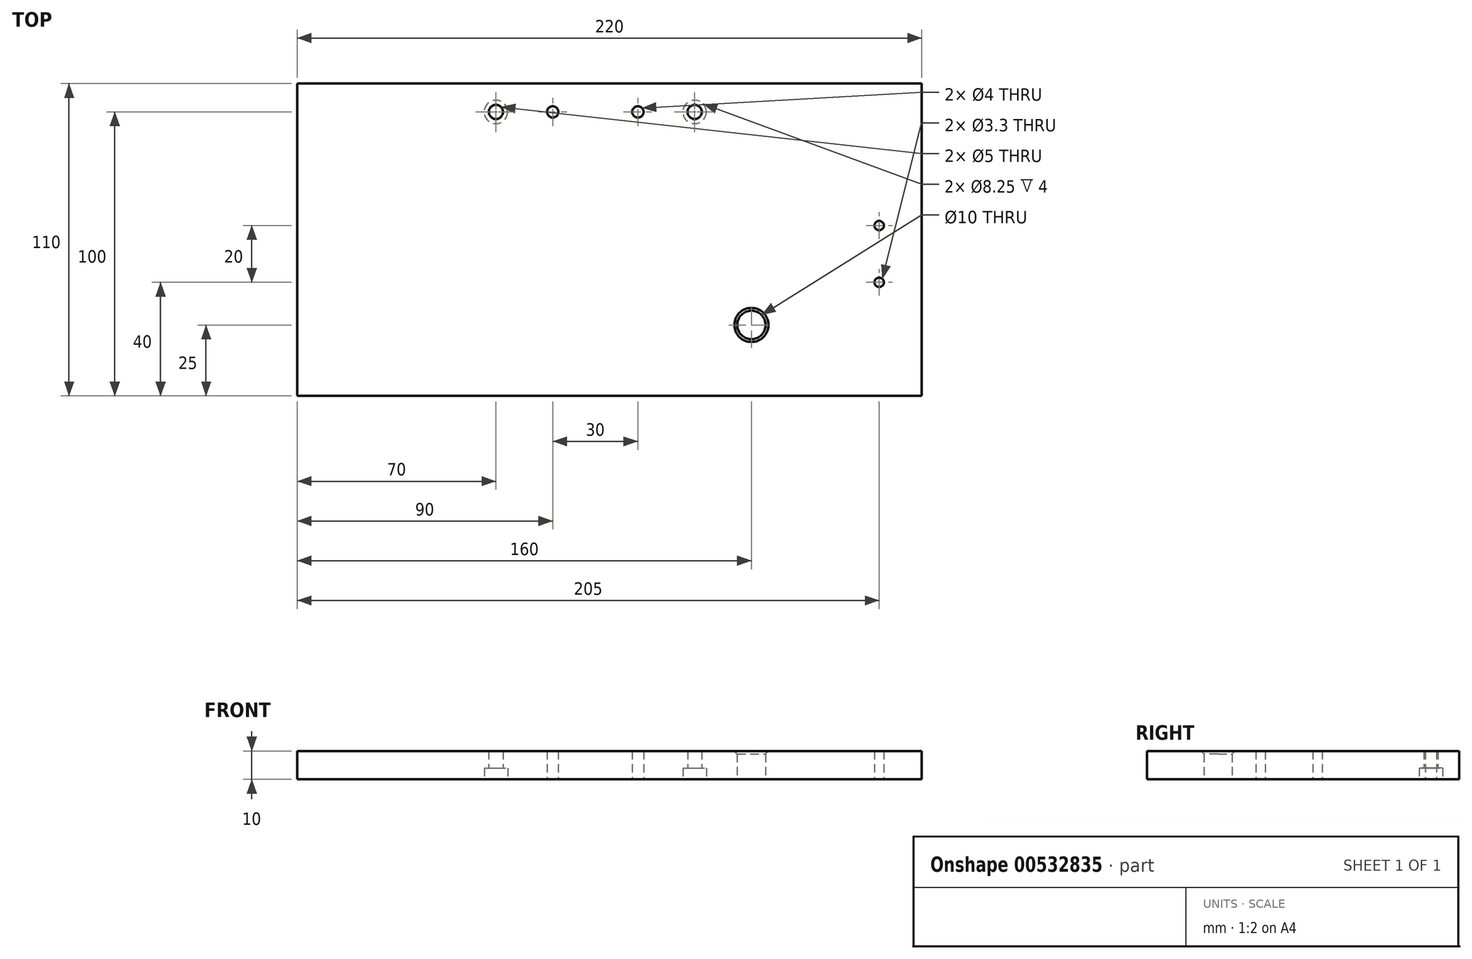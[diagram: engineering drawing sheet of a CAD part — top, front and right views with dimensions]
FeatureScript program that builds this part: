
annotation { "Feature Type Name" : "Feature", "Feature Type Description" : "" }
export const myFeature = defineFeature(function(context is Context, id is Id, definition is map)
    precondition{}
    {
        {
            var Q0;
            Q0=qCreatedBy(makeId("Top.planeOp"),FACE);
            var sketch = newSketch(context, id + "F0", { "sketchPlane" : qUnion([Q0])});
            skLineSegment(sketch, "E0.bottom", {"start": v(-110, 55) * mm, "end": v(110, 55) * mm});
            skLineSegment(sketch, "E0.top", {"start": v(-110, -55) * mm, "end": v(110, -55) * mm});
            skLineSegment(sketch, "E0.left", {"start": v(-110, 55) * mm, "end": v(-110, -55) * mm});
            skLineSegment(sketch, "E0.right", {"start": v(110, 55) * mm, "end": v(110, -55) * mm});
            skSolve(sketch);
        }
        {
            var Q0;
            Q0 = qSketchRegion(id + "F0", true);
            extrude(context, id + "F1", {"entities" : qUnion([Q0]), "depth" : 10 * mm, "offsetDistance" : 25 * mm});
        }
        {
            var Q0;
            Q0=makeQuery(id+"F1.opExtrude","CAP_FACE",FACE,{"disambiguationData":[OSD([sQuery(id+"F0.wireOp",EDGE,"E0.bottom"),sQuery(id+"F0.wireOp",EDGE,"E0.top"),sQuery(id+"F0.wireOp",EDGE,"E0.left"),sQuery(id+"F0.wireOp",EDGE,"E0.right")])],"isStart":true});
            var sketch = newSketch(context, id + "F2", { "sketchPlane" : qUnion([Q0])});
            skPoint(sketch, "E1", {"position": v(95, 15) * mm});
            skPoint(sketch, "E2", {"position": v(95, -5) * mm});
            skPoint(sketch, "E3", {"position": v(-40, -45) * mm});
            skPoint(sketch, "E4", {"position": v(30, -45) * mm});
            skPoint(sketch, "E5", {"position": v(-20, -45) * mm});
            skPoint(sketch, "E6", {"position": v(10, -45) * mm});
            skCircle(sketch, "E7", {"center": v(50, 30) * mm, "radius": 5 * mm});
            skCircle(sketch, "E8", {"center": v(-20, -45) * mm, "radius": 2 * mm});
            skCircle(sketch, "E9", {"center": v(10, -45) * mm, "radius": 2 * mm});
            skSolve(sketch);
        }
        {
            var Q0;
            Q0=makeQuery(id+"F2.imprint","IMPRINT",FACE,{"disambiguationData":[TD([[makeQuery(id+"F2.imprint","IMPRINT",EDGE,{"derivedFrom":sQuery(id+"F2.wireOp",EDGE,"E7")}),1.0]])]});
            var Q1;
            Q1=makeQuery(id+"F2.imprint","IMPRINT",FACE,{"disambiguationData":[TD([[makeQuery(id+"F2.imprint","IMPRINT",EDGE,{"derivedFrom":sQuery(id+"F2.wireOp",EDGE,"E8")}),1.0]])]});
            var Q2;
            Q2=makeQuery(id+"F2.imprint","IMPRINT",FACE,{"disambiguationData":[TD([[makeQuery(id+"F2.imprint","IMPRINT",EDGE,{"derivedFrom":sQuery(id+"F2.wireOp",EDGE,"E9")}),1.0]])]});
            extrude(context, id + "F3", {"entities" : qUnion([Q0, Q1, Q2]), "operationType" : NewBodyOperationType.REMOVE, "endBound" : BoundingType.THROUGH_ALL, "oppositeDirection" : true, "depth" : 25 * mm, "offsetDistance" : 25 * mm});
        }
        {
            var Q0;
            Q0=sQuery(id+"F2.wireOp",VERTEX,"E2");
            var Q1;
            Q1=sQuery(id+"F2.wireOp",VERTEX,"E1");
            var Q2;
            Q2=makeQuery(id+"F1.opExtrude","SWEPT_BODY",BODY,{"disambiguationData":[OSD([sQuery(id+"F0.wireOp",EDGE,"E0.bottom"),sQuery(id+"F0.wireOp",EDGE,"E0.top"),sQuery(id+"F0.wireOp",EDGE,"E0.left"),sQuery(id+"F0.wireOp",EDGE,"E0.right")])]});
            hole(context, id + "F4", {"style" : HoleStyle.SIMPLE, "endStyle" : HoleEndStyle.THROUGH, "standardTappedOrClearance" : lookupTablePath({ "standard" : "ISO", "engagement" : "75%", "pitch" : "0.7 mm", "size" : "M4", "type" : "Tapped" }), "standardBlindInLast" : lookupTablePath({ "standard" : "ISO", "engagement" : "75%", "pitch" : "0.7 mm", "size" : "M4", "type" : "Tapped" }), "holeDiameter" : 3.3 * mm, "showTappedDepth" : true, "isTappedThrough" : true, "tappedDepth" : 12 * mm, "tapClearance" : 3, "locations" : qUnion([Q0, Q1]), "scope" : qUnion([Q2]), "majorDiameter" : 4 * mm});
        }
        {
            var Q0;
            Q0=sQuery(id+"F2.wireOp",VERTEX,"E3");
            var Q1;
            Q1=sQuery(id+"F2.wireOp",VERTEX,"E4");
            var Q2;
            Q2=makeQuery(id+"F1.opExtrude","SWEPT_BODY",BODY,{"disambiguationData":[OSD([sQuery(id+"F0.wireOp",EDGE,"E0.bottom"),sQuery(id+"F0.wireOp",EDGE,"E0.top"),sQuery(id+"F0.wireOp",EDGE,"E0.left"),sQuery(id+"F0.wireOp",EDGE,"E0.right")])]});
            hole(context, id + "F5", {"style" : HoleStyle.C_BORE, "endStyle" : HoleEndStyle.THROUGH, "standardTappedOrClearance" : lookupTablePath({ "standard" : "ISO", "size" : "5", "type" : "Drilled" }), "standardBlindInLast" : lookupTablePath({ "standard" : "ISO", "size" : "5", "type" : "Drilled" }), "holeDiameter" : 5 * mm, "cBoreDiameter" : 8.25 * mm, "cBoreDepth" : 4 * mm, "isTappedThrough" : true, "tappedDepth" : 12 * mm, "tapClearance" : 3, "locations" : qUnion([Q0, Q1]), "scope" : qUnion([Q2])});
        }
        {
            var Q0;
            Q0=makeQuery(id+"F3.boolean.opBoolean","INTERSECT",EDGE,{"derivedFrom":[makeQuery(id+"F1.opExtrude","CAP_FACE",FACE,{"disambiguationData":[OSD([sQuery(id+"F0.wireOp",EDGE,"E0.bottom"),sQuery(id+"F0.wireOp",EDGE,"E0.top"),sQuery(id+"F0.wireOp",EDGE,"E0.left"),sQuery(id+"F0.wireOp",EDGE,"E0.right")])],"isStart":false}),makeQuery(id+"F3.opExtrude","SWEPT_FACE",FACE,{"disambiguationData":[OSD([sQuery(id+"F2.wireOp",EDGE,"E7")])]})]});
            chamfer(context, id + "F6", {"entities" : qUnion([Q0]), "width" : 1 * mm, "tangentPropagation" : true});
        }
    });
